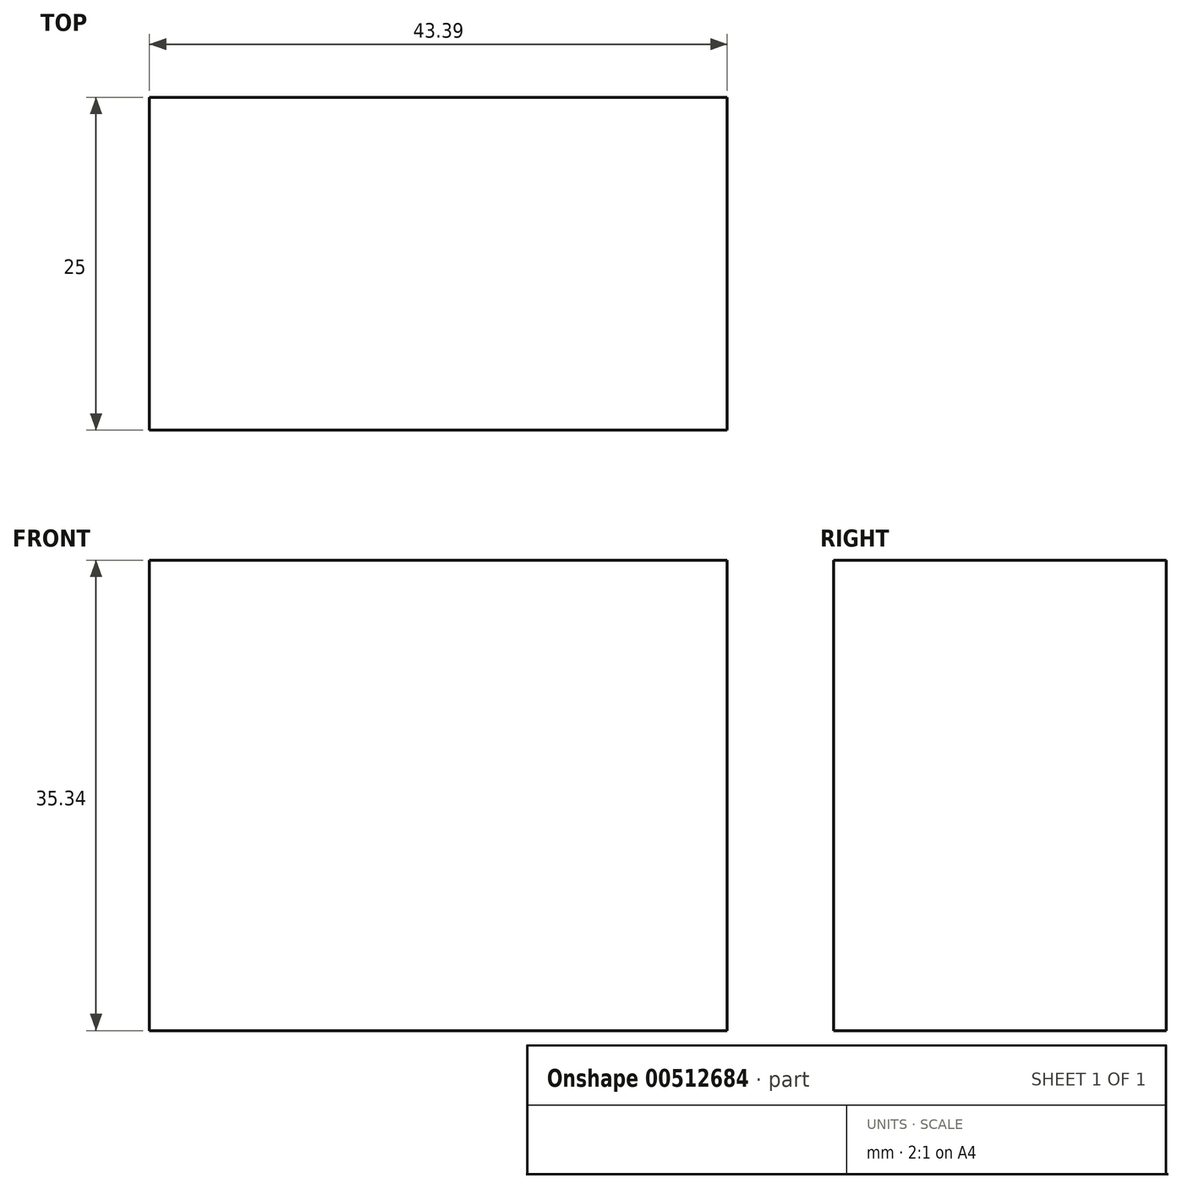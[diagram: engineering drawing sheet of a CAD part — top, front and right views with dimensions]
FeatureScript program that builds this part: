
annotation { "Feature Type Name" : "Feature", "Feature Type Description" : "" }
export const myFeature = defineFeature(function(context is Context, id is Id, definition is map)
    precondition{}
    {
        {
            var Q0;
            Q0=qCreatedBy(makeId("Front.planeOp"),FACE);
            var sketch = newSketch(context, id + "F0", { "sketchPlane" : qUnion([Q0])});
            skLineSegment(sketch, "E0.bottom", {"start": v(-93.46, 0) * mm, "end": v(-50.07, 0) * mm});
            skLineSegment(sketch, "E0.top", {"start": v(-93.46, 35.34) * mm, "end": v(-50.07, 35.34) * mm});
            skLineSegment(sketch, "E0.left", {"start": v(-93.46, 0) * mm, "end": v(-93.46, 35.34) * mm});
            skLineSegment(sketch, "E0.right", {"start": v(-50.07, 0) * mm, "end": v(-50.07, 35.34) * mm});
            skPoint(sketch, "E0.middle", {"position": v(-71.76, 17.67) * mm});
            skSolve(sketch);
        }
        {
            var Q0;
            Q0=makeQuery(id+"F0.imprint","IMPRINT",FACE,{"disambiguationData":[TD([[makeQuery(id+"F0.imprint","IMPRINT",EDGE,{"derivedFrom":sQuery(id+"F0.wireOp",EDGE,"E0.bottom")}),1.0]])]});
            extrude(context, id + "F1", {"entities" : qUnion([Q0]), "depth" : 25 * mm});
        }
    });
